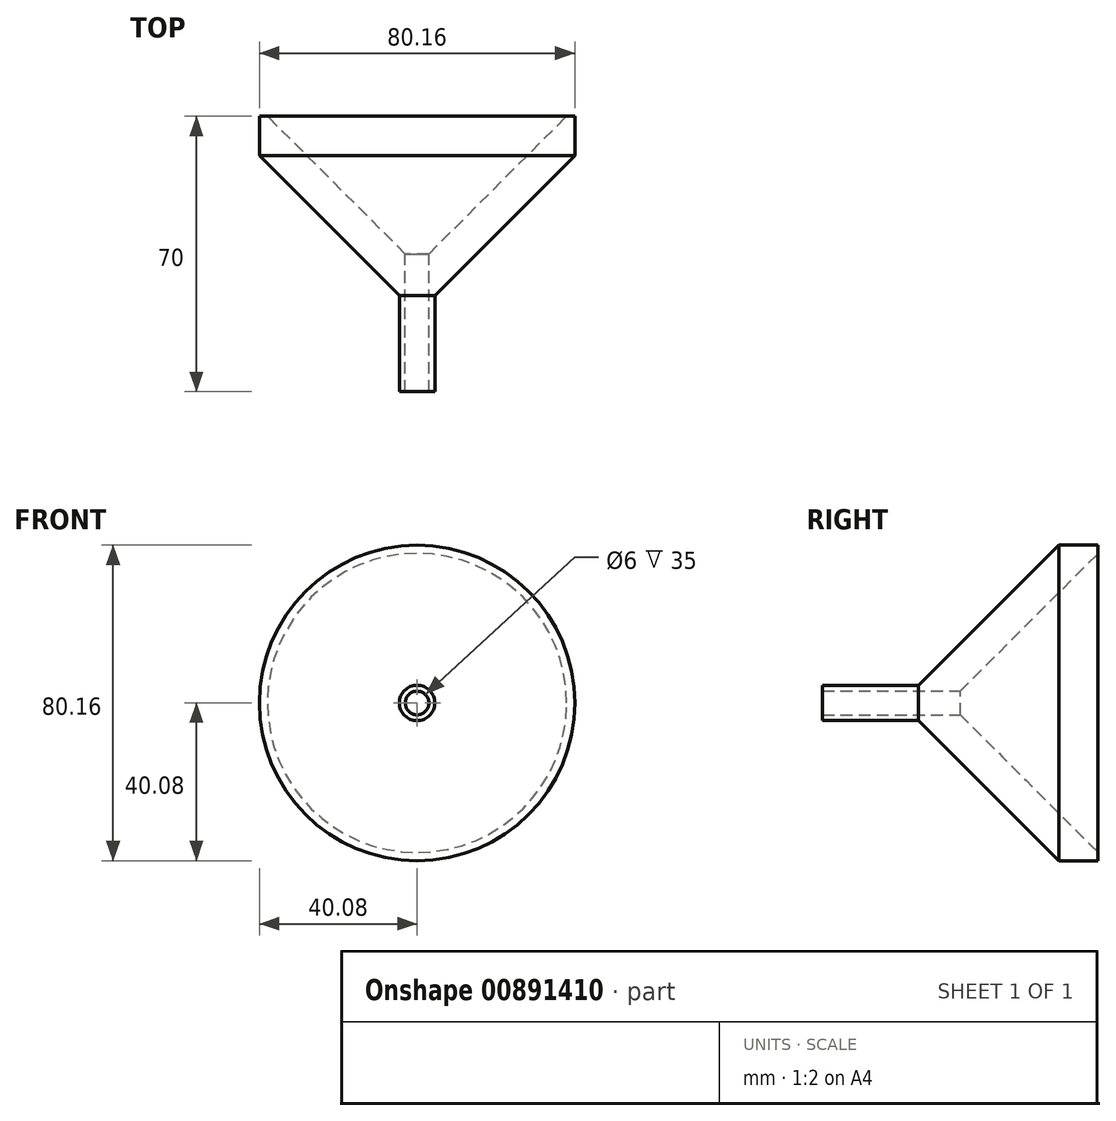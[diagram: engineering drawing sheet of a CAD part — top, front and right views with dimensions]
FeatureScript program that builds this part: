
annotation { "Feature Type Name" : "Feature", "Feature Type Description" : "" }
export const myFeature = defineFeature(function(context is Context, id is Id, definition is map)
    precondition{}
    {
        {
            var Q0;
            Q0=qCreatedBy(makeId("Front.planeOp"),FACE);
            var sketch = newSketch(context, id + "F0", { "sketchPlane" : qUnion([Q0])});
            skCircle(sketch, "E0", {"center": v(0, 0) * mm, "radius": 3 * mm});
            skCircle(sketch, "E1", {"center": v(0, 0) * mm, "radius": 4.5 * mm});
            skCircle(sketch, "E2", {"center": v(0, 0) * mm, "radius": 40.08 * mm});
            skSolve(sketch);
        }
        {
            var Q0;
            Q0=makeQuery(id+"F0.imprint","IMPRINT",FACE,{"disambiguationData":[TD([[makeQuery(id+"F0.imprint","IMPRINT",EDGE,{"derivedFrom":sQuery(id+"F0.wireOp",EDGE,"E1")}),-1.0]])]});
            extrude(context, id + "F1", {"entities" : qUnion([Q0]), "depth" : 50 * mm, "offsetDistance" : 25 * mm});
        }
        {
            var Q0;
            Q0=makeQuery(id+"F1.opExtrude","CAP_EDGE",EDGE,{"disambiguationData":[OSD([sQuery(id+"F0.wireOp",EDGE,"E2")])],"isStart":false});
            chamfer(context, id + "F2", {"entities" : qUnion([Q0]), "width" : 40 * mm, "tangentPropagation" : true});
        }
        {
            var Q0;
            Q0=makeQuery(id+"F0.imprint","IMPRINT",FACE,{"disambiguationData":[TD([[makeQuery(id+"F0.imprint","IMPRINT",EDGE,{"derivedFrom":sQuery(id+"F0.wireOp",EDGE,"E0")}),-1.0]])]});
            extrude(context, id + "F3", {"entities" : qUnion([Q0]), "operationType" : NewBodyOperationType.ADD, "depth" : 70 * mm, "offsetDistance" : 25 * mm});
        }
        {
            var Q0;
            Q0=makeQuery(id+"F3.opExtrude","CAP_EDGE",EDGE,{"disambiguationData":[OSD([sQuery(id+"F0.wireOp",EDGE,"E0")])],"isStart":true});
            chamfer(context, id + "F4", {"entities" : qUnion([Q0]), "width" : 35 * mm, "tangentPropagation" : true});
        }
    });
